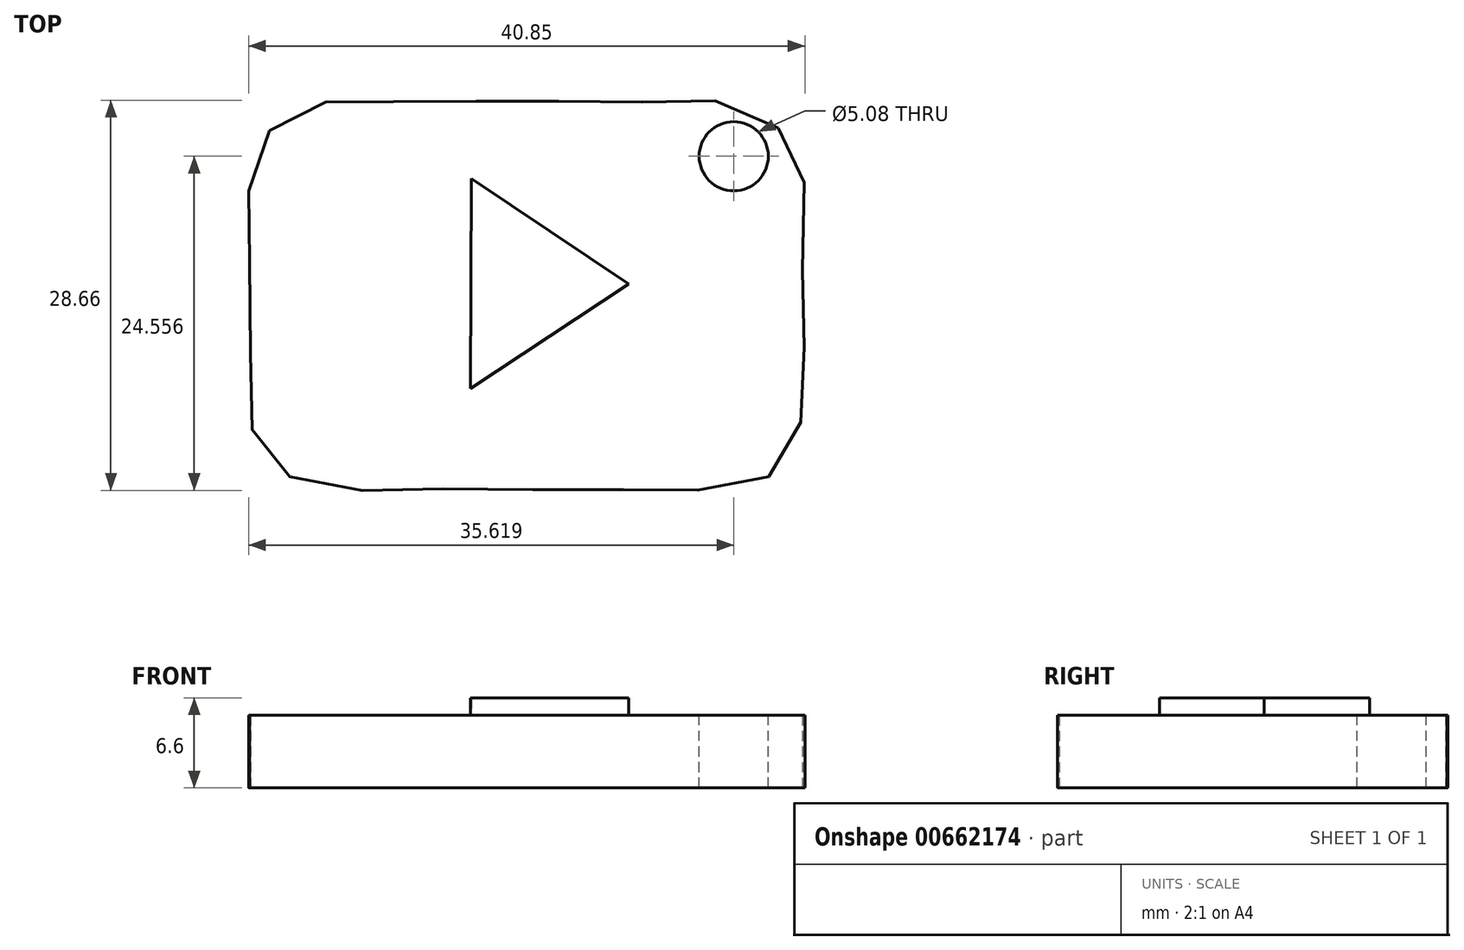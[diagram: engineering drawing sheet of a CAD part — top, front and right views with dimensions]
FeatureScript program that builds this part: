
annotation { "Feature Type Name" : "Feature", "Feature Type Description" : "" }
export const myFeature = defineFeature(function(context is Context, id is Id, definition is map)
    precondition{}
    {
        {
            var Q0;
            Q0=qCreatedBy(makeId("Top.planeOp"),FACE);
            var sketch = newSketch(context, id + "F0", { "sketchPlane" : qUnion([Q0])});
            skFitSpline(sketch, "E0", {"points": [v(-53.34, 36.6) * mm, v(-49.57, 36.67) * mm, v(-43.89, 36.67) * mm, v(-37.85, 36.67) * mm, v(-31.75, 36.64) * mm, v(-26.38, 36.6) * mm, v(-22.74, 36.4) * mm, v(-19.07, 33.55) * mm, v(-18.2, 30.72) * mm, v(-18.33, 23.99) * mm, v(-18.2, 18.8) * mm, v(-18.33, 13.82) * mm, v(-19.7, 10.11) * mm, v(-22.64, 8.32) * mm, v(-27.97, 8.14) * mm, v(-32.72, 8.12) * mm, v(-40.65, 8.17) * mm, v(-46.89, 8.17) * mm, v(-52.42, 8.17) * mm, v(-56.62, 9.46) * mm, v(-58.61, 12) * mm, v(-58.91, 16.15) * mm, v(-58.91, 23.73) * mm, v(-59, 28.32) * mm, v(-58.61, 32.66) * mm, v(-56.68, 35.2) * mm, v(-53.34, 36.6) * mm]});
            skSolve(sketch);
        }
        {
            var Q0;
            Q0=makeQuery(id+"F0.imprint","IMPRINT",FACE,{"disambiguationData":[TD([[makeQuery(id+"F0.imprint","IMPRINT",EDGE,{"derivedFrom":sQuery(id+"F0.wireOp",EDGE,"E0")}),-1.0]])]});
            var sketch = newSketch(context, id + "F1", { "sketchPlane" : qUnion([Q0])});
            skLineSegment(sketch, "E1", {"start": v(-42.65, 31) * mm, "end": v(-31.08, 23.23) * mm});
            skLineSegment(sketch, "E2", {"start": v(-31.08, 23.23) * mm, "end": v(-42.72, 15.55) * mm});
            skLineSegment(sketch, "E3", {"start": v(-42.72, 15.55) * mm, "end": v(-42.65, 31) * mm});
            skSolve(sketch);
        }
        {
            var Q0;
            Q0 = qSketchRegion(id + "F0", true);
            extrude(context, id + "F2", {"entities" : qUnion([Q0]), "depth" : 5.33 * mm, "offsetDistance" : 25.4 * mm});
        }
        {
            var Q0;
            Q0 = qSketchRegion(id + "F1", true);
            extrude(context, id + "F3", {"entities" : qUnion([Q0]), "operationType" : NewBodyOperationType.ADD, "depth" : 6.6 * mm, "offsetDistance" : 25.4 * mm});
        }
        {
            var Q0;
            Q0=makeQuery(id+"F2.opExtrude","CAP_FACE",FACE,{"disambiguationData":[OSD([sQuery(id+"F0.wireOp",EDGE,"E0")])],"isStart":false});
            var sketch = newSketch(context, id + "F4", { "sketchPlane" : qUnion([Q0])});
            skCircle(sketch, "E4", {"center": v(-23.38, 32.63) * mm, "radius": 2.7 * mm});
            skSolve(sketch);
        }
        {
            var Q0;
            Q0=sQuery(id+"F4.wireOp",VERTEX,"E4.center");
            var Q1;
            Q1=makeQuery(id+"F2.opExtrude","SWEPT_BODY",BODY,{"disambiguationData":[OSD([sQuery(id+"F0.wireOp",EDGE,"E0")])]});
            hole(context, id + "F5", {"style" : HoleStyle.SIMPLE, "endStyle" : HoleEndStyle.THROUGH, "holeDiameter" : 5.08 * mm, "majorDiameter" : 6.35 * mm, "isTappedThrough" : true, "tappedDepth" : 12.7 * mm, "tapClearance" : 3, "locations" : qUnion([Q0]), "scope" : qUnion([Q1])});
        }
    });
